# Revit family: Legrand Kit Colonnes Ovaline
name_source: partatom
category: Installations électriques
units: mm (PartAtom-declared; Revit-internal decimal feet)

## family parameters
Conserver l'orientation des annotations = Non
Cote de connecteur circulaire = Utiliser le diamètre
Couper avec des vides une fois chargée = Non
Hôte = Face
Partagée = Non
Point de calcul de pièce = Non
Type d'élément = Normal

## types (4) — shared parameters
Fabricant = LEGRAND
Matériau principal = Aluminium
Nombre de compartiments = Autre
Standard = Ovaline
h1 = 2700 mm  [stored 8.85827 ft]
zero-valued in all types: Elévation par défaut

## per-type parameters (varying)
| type | Description | Finition | Modèle |
| Kit Ovaline Colonnette 1C Blanc | kit extension Colonnette 1cpt45 Blanche  Ovaline 2,67m +chapeau +cloison+cache plaf | Blanc | LG-653060 |
| Kit Ovaline Colonnette 1C Noir | kit extension Colonnette 1cpt45 Noir  Ovaline 2,67m +chapeau +cloison +cache fix | Noir | LG-653062 |
| Kit Ovaline Colonnette T2 Blanc | kit extension Colonnette Blanc 2cpt45 ou 1cpt 80 Ovaline 2,67m +chap +cloi +cach | Blanc | LG-653063 |
| Kit Ovaline Colonnette T2 Noir | kit extension Colonnette Noir 2cpt 45 ou 1cpt 80 Ovaline 2,67m +chap +cloi +cach | Noir | LG-653065 |

note: [stored X ft] marks values corroborated as IEEE doubles in the binary element streams (Revit-internal decimal feet)
